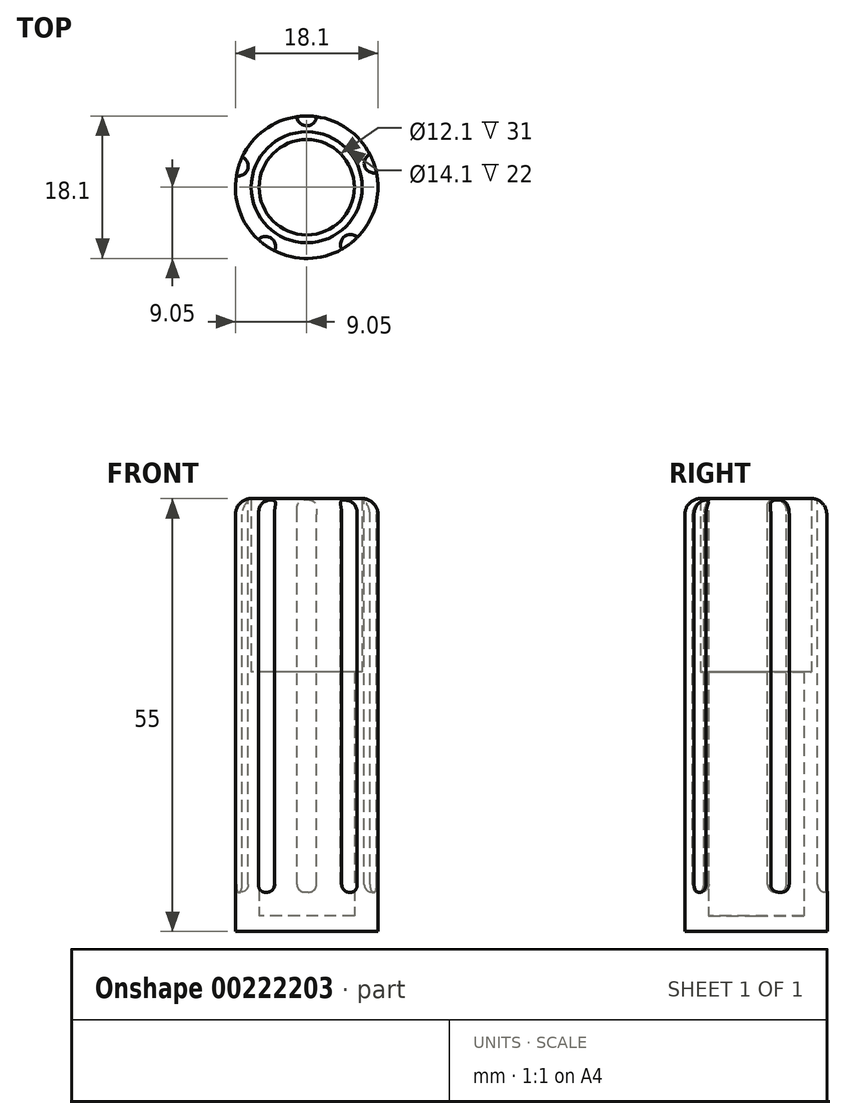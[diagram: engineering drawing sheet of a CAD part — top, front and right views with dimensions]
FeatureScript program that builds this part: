
annotation { "Feature Type Name" : "Feature", "Feature Type Description" : "" }
export const myFeature = defineFeature(function(context is Context, id is Id, definition is map)
    precondition{}
    {
        {
            var Q0;
            Q0=qCreatedBy(makeId("Top.planeOp"),FACE);
            var sketch = newSketch(context, id + "F0", { "sketchPlane" : qUnion([Q0])});
            skCircle(sketch, "E0", {"center": v(0, 0) * mm, "radius": 6.05 * mm});
            skCircle(sketch, "E1", {"center": v(0, 0) * mm, "radius": 7.05 * mm});
            skCircle(sketch, "E2", {"center": v(0, 0) * mm, "radius": 9.05 * mm});
            skCircle(sketch, "E3", {"center": v(0, 9.05) * mm, "radius": 1.25 * mm});
            skCircle(sketch, "E4.1.0", {"center": v(-8.68, 2.69) * mm, "radius": 1.25 * mm});
            skCircle(sketch, "E4.2.0", {"center": v(-5.22, -7.5) * mm, "radius": 1.25 * mm});
            skCircle(sketch, "E4.3.0", {"center": v(5.54, -7.27) * mm, "radius": 1.25 * mm});
            skCircle(sketch, "E4.4.0", {"center": v(8.55, 3.06) * mm, "radius": 1.25 * mm});
            skPoint(sketch, "E4.center", {"position": v(0, -0.05) * mm});
            skLineSegment(sketch, "E4.anchor1", {"start": v(0, -0.05) * mm, "end": v(0, 9.05) * mm, "construction": true});
            skLineSegment(sketch, "E4.anchor2", {"start": v(0, -0.05) * mm, "end": v(8.55, 3.06) * mm, "construction": true});
            skSolve(sketch);
        }
        {
            var Q0;
            Q0=makeQuery(id+"F0.imprint","IMPRINT",FACE,{"disambiguationData":[TD([[makeQuery(id+"F0.imprint","IMPRINT",EDGE,{"derivedFrom":sQuery(id+"F0.wireOp",EDGE,"E0")}),1.0]])]});
            var Q1;
            Q1=makeQuery(id+"F0.imprint","IMPRINT",FACE,{"disambiguationData":[TD([[makeQuery(id+"F0.imprint","IMPRINT",EDGE,{"derivedFrom":sQuery(id+"F0.wireOp",EDGE,"E0")}),-1.0]])]});
            var Q2;
            Q2=makeQuery(id+"F0.imprint","IMPRINT",FACE,{"disambiguationData":[TD([[makeQuery(id+"F0.imprint","IMPRINT",EDGE,{"derivedFrom":sQuery(id+"F0.wireOp",EDGE,"E1")}),-1.0]])]});
            extrude(context, id + "F1", {"entities" : qUnion([Q0, Q1, Q2]), "oppositeDirection" : true, "depth" : 2 * mm});
        }
        {
            var Q0;
            Q0=makeQuery(id+"F0.imprint","IMPRINT",FACE,{"disambiguationData":[TD([[makeQuery(id+"F0.imprint","IMPRINT",EDGE,{"derivedFrom":sQuery(id+"F0.wireOp",EDGE,"E0")}),-1.0]])]});
            extrude(context, id + "F2", {"entities" : qUnion([Q0]), "operationType" : NewBodyOperationType.ADD, "depth" : 31 * mm});
        }
        {
            var Q0;
            Q0=makeQuery(id+"F0.imprint","IMPRINT",FACE,{"disambiguationData":[TD([[makeQuery(id+"F0.imprint","IMPRINT",EDGE,{"derivedFrom":sQuery(id+"F0.wireOp",EDGE,"E1")}),-1.0]])]});
            extrude(context, id + "F3", {"entities" : qUnion([Q0]), "operationType" : NewBodyOperationType.ADD, "depth" : 53 * mm});
        }
        {
            var Q0;
            {var subQ0=sQuery(id+"F0.wireOp",EDGE,"E2");Q0=makeQuery(id+"F3.opExtrude","CAP_EDGE",EDGE,{"disambiguationData":[OSD([subQ0]),TDD([makeQuery(id+"F0.imprint","IMPRINT",EDGE,{"disambiguationData":[TD([[makeQuery(id+"F0.imprint","INTERSECT",VERTEX,{"disambiguationData":[OD(1.0)],"derivedFrom":[subQ0,sQuery(id+"F0.wireOp",EDGE,"E4.1.0")]}),-1.0]])],"derivedFrom":subQ0})])],"isStart":false});}
            var Q1;
            {var subQ0=sQuery(id+"F0.wireOp",EDGE,"E2");Q1=makeQuery(id+"F3.opExtrude","CAP_EDGE",EDGE,{"disambiguationData":[OSD([subQ0]),TDD([makeQuery(id+"F0.imprint","IMPRINT",EDGE,{"disambiguationData":[TD([[makeQuery(id+"F0.imprint","INTERSECT",VERTEX,{"disambiguationData":[OD(1.0)],"derivedFrom":[subQ0,sQuery(id+"F0.wireOp",EDGE,"E4.2.0")]}),-1.0]])],"derivedFrom":subQ0})])],"isStart":false});}
            var Q2;
            {var subQ0=sQuery(id+"F0.wireOp",EDGE,"E2");Q2=makeQuery(id+"F3.opExtrude","CAP_EDGE",EDGE,{"disambiguationData":[OSD([subQ0]),TDD([makeQuery(id+"F0.imprint","IMPRINT",EDGE,{"disambiguationData":[TD([[makeQuery(id+"F0.imprint","INTERSECT",VERTEX,{"disambiguationData":[OD(1.0)],"derivedFrom":[subQ0,sQuery(id+"F0.wireOp",EDGE,"E3")]}),-1.0]])],"derivedFrom":subQ0})])],"isStart":false});}
            var Q3;
            {var subQ0=sQuery(id+"F0.wireOp",EDGE,"E2");Q3=makeQuery(id+"F3.opExtrude","CAP_EDGE",EDGE,{"disambiguationData":[OSD([subQ0]),TDD([makeQuery(id+"F0.imprint","IMPRINT",EDGE,{"disambiguationData":[TD([[makeQuery(id+"F0.imprint","INTERSECT",VERTEX,{"disambiguationData":[OD(0.0)],"derivedFrom":[subQ0,sQuery(id+"F0.wireOp",EDGE,"E4.4.0")]}),-1.0]])],"derivedFrom":subQ0})])],"isStart":false});}
            var Q4;
            {var subQ0=sQuery(id+"F0.wireOp",EDGE,"E2");Q4=makeQuery(id+"F3.opExtrude","CAP_EDGE",EDGE,{"disambiguationData":[OSD([subQ0]),TDD([makeQuery(id+"F0.imprint","IMPRINT",EDGE,{"disambiguationData":[TD([[makeQuery(id+"F0.imprint","INTERSECT",VERTEX,{"disambiguationData":[OD(1.0)],"derivedFrom":[subQ0,sQuery(id+"F0.wireOp",EDGE,"E4.4.0")]}),1.0]])],"derivedFrom":subQ0})])],"isStart":false});}
            fillet(context, id + "F4", {"entities" : qUnion([Q0, Q1, Q2, Q3, Q4]), "radius" : 2 * mm, "tangentPropagation" : true, "allowEdgeOverflow" : false});
        }
        {
            var Q0;
            {var subQ0=sQuery(id+"F0.wireOp",EDGE,"E4.4.0");var subQ1=sQuery(id+"F0.wireOp",EDGE,"E2");var subQ2=makeQuery(id+"F0.imprint","INTERSECT",VERTEX,{"disambiguationData":[OD(0.0)],"derivedFrom":[subQ1,subQ0]});Q0=makeQuery(id+"F0.imprint","IMPRINT",FACE,{"disambiguationData":[TD([[makeQuery(id+"F0.imprint","IMPRINT",EDGE,{"disambiguationData":[TD([[subQ2,1.0]])],"derivedFrom":subQ1}),1.0]])]});}
            var Q1;
            {var subQ0=sQuery(id+"F0.wireOp",EDGE,"E4.3.0");var subQ1=sQuery(id+"F0.wireOp",EDGE,"E2");var subQ2=makeQuery(id+"F0.imprint","INTERSECT",VERTEX,{"disambiguationData":[OD(0.0)],"derivedFrom":[subQ1,subQ0]});Q1=makeQuery(id+"F0.imprint","IMPRINT",FACE,{"disambiguationData":[TD([[makeQuery(id+"F0.imprint","IMPRINT",EDGE,{"disambiguationData":[TD([[subQ2,-1.0]])],"derivedFrom":subQ1}),1.0]])]});}
            var Q2;
            {var subQ0=sQuery(id+"F0.wireOp",EDGE,"E4.2.0");var subQ1=sQuery(id+"F0.wireOp",EDGE,"E2");var subQ2=makeQuery(id+"F0.imprint","INTERSECT",VERTEX,{"disambiguationData":[OD(0.0)],"derivedFrom":[subQ1,subQ0]});Q2=makeQuery(id+"F0.imprint","IMPRINT",FACE,{"disambiguationData":[TD([[makeQuery(id+"F0.imprint","IMPRINT",EDGE,{"disambiguationData":[TD([[subQ2,-1.0]])],"derivedFrom":subQ1}),1.0]])]});}
            var Q3;
            {var subQ0=sQuery(id+"F0.wireOp",EDGE,"E4.1.0");var subQ1=sQuery(id+"F0.wireOp",EDGE,"E2");var subQ2=makeQuery(id+"F0.imprint","INTERSECT",VERTEX,{"disambiguationData":[OD(0.0)],"derivedFrom":[subQ1,subQ0]});Q3=makeQuery(id+"F0.imprint","IMPRINT",FACE,{"disambiguationData":[TD([[makeQuery(id+"F0.imprint","IMPRINT",EDGE,{"disambiguationData":[TD([[subQ2,-1.0]])],"derivedFrom":subQ1}),1.0]])]});}
            var Q4;
            {var subQ0=sQuery(id+"F0.wireOp",EDGE,"E3");var subQ1=sQuery(id+"F0.wireOp",EDGE,"E2");var subQ2=makeQuery(id+"F0.imprint","INTERSECT",VERTEX,{"disambiguationData":[OD(0.0)],"derivedFrom":[subQ1,subQ0]});Q4=makeQuery(id+"F0.imprint","IMPRINT",FACE,{"disambiguationData":[TD([[makeQuery(id+"F0.imprint","IMPRINT",EDGE,{"disambiguationData":[TD([[subQ2,-1.0]])],"derivedFrom":subQ1}),1.0]])]});}
            extrude(context, id + "F5", {"entities" : qUnion([Q0, Q1, Q2, Q3, Q4]), "operationType" : NewBodyOperationType.ADD, "depth" : 3 * mm});
        }
        {
            var Q0;
            Q0=makeQuery(id+"F5.opExtrude","CAP_EDGE",EDGE,{"disambiguationData":[OSD([sQuery(id+"F0.wireOp",EDGE,"E4.2.0")])],"isStart":false});
            var Q1;
            Q1=makeQuery(id+"F5.opExtrude","CAP_EDGE",EDGE,{"disambiguationData":[OSD([sQuery(id+"F0.wireOp",EDGE,"E4.1.0")])],"isStart":false});
            var Q2;
            Q2=makeQuery(id+"F5.opExtrude","CAP_EDGE",EDGE,{"disambiguationData":[OSD([sQuery(id+"F0.wireOp",EDGE,"E4.3.0")])],"isStart":false});
            var Q3;
            Q3=makeQuery(id+"F5.opExtrude","CAP_EDGE",EDGE,{"disambiguationData":[OSD([sQuery(id+"F0.wireOp",EDGE,"E4.4.0")])],"isStart":false});
            var Q4;
            Q4=makeQuery(id+"F5.opExtrude","CAP_EDGE",EDGE,{"disambiguationData":[OSD([sQuery(id+"F0.wireOp",EDGE,"E3")])],"isStart":false});
            fillet(context, id + "F6", {"entities" : qUnion([Q0, Q1, Q2, Q3, Q4]), "radius" : 1 * mm, "tangentPropagation" : true, "allowEdgeOverflow" : false});
        }
        {
            var Q0;
            {var subQ0=sQuery(id+"F0.wireOp",EDGE,"E4.2.0");var subQ1=sQuery(id+"F0.wireOp",EDGE,"E2");var subQ2=makeQuery(id+"F0.imprint","INTERSECT",VERTEX,{"disambiguationData":[OD(0.0)],"derivedFrom":[subQ1,subQ0]});Q0=makeQuery(id+"F0.imprint","IMPRINT",FACE,{"disambiguationData":[TD([[makeQuery(id+"F0.imprint","IMPRINT",EDGE,{"disambiguationData":[TD([[subQ2,-1.0]])],"derivedFrom":subQ1}),1.0]])]});}
            var Q1;
            {var subQ0=sQuery(id+"F0.wireOp",EDGE,"E4.3.0");var subQ1=sQuery(id+"F0.wireOp",EDGE,"E2");var subQ2=makeQuery(id+"F0.imprint","INTERSECT",VERTEX,{"disambiguationData":[OD(0.0)],"derivedFrom":[subQ1,subQ0]});Q1=makeQuery(id+"F0.imprint","IMPRINT",FACE,{"disambiguationData":[TD([[makeQuery(id+"F0.imprint","IMPRINT",EDGE,{"disambiguationData":[TD([[subQ2,-1.0]])],"derivedFrom":subQ1}),1.0]])]});}
            var Q2;
            {var subQ0=sQuery(id+"F0.wireOp",EDGE,"E4.4.0");var subQ1=sQuery(id+"F0.wireOp",EDGE,"E2");var subQ2=makeQuery(id+"F0.imprint","INTERSECT",VERTEX,{"disambiguationData":[OD(0.0)],"derivedFrom":[subQ1,subQ0]});Q2=makeQuery(id+"F0.imprint","IMPRINT",FACE,{"disambiguationData":[TD([[makeQuery(id+"F0.imprint","IMPRINT",EDGE,{"disambiguationData":[TD([[subQ2,1.0]])],"derivedFrom":subQ1}),1.0]])]});}
            var Q3;
            {var subQ0=sQuery(id+"F0.wireOp",EDGE,"E3");var subQ1=sQuery(id+"F0.wireOp",EDGE,"E2");var subQ2=makeQuery(id+"F0.imprint","INTERSECT",VERTEX,{"disambiguationData":[OD(0.0)],"derivedFrom":[subQ1,subQ0]});Q3=makeQuery(id+"F0.imprint","IMPRINT",FACE,{"disambiguationData":[TD([[makeQuery(id+"F0.imprint","IMPRINT",EDGE,{"disambiguationData":[TD([[subQ2,-1.0]])],"derivedFrom":subQ1}),1.0]])]});}
            var Q4;
            {var subQ0=sQuery(id+"F0.wireOp",EDGE,"E4.1.0");var subQ1=sQuery(id+"F0.wireOp",EDGE,"E2");var subQ2=makeQuery(id+"F0.imprint","INTERSECT",VERTEX,{"disambiguationData":[OD(0.0)],"derivedFrom":[subQ1,subQ0]});Q4=makeQuery(id+"F0.imprint","IMPRINT",FACE,{"disambiguationData":[TD([[makeQuery(id+"F0.imprint","IMPRINT",EDGE,{"disambiguationData":[TD([[subQ2,-1.0]])],"derivedFrom":subQ1}),1.0]])]});}
            extrude(context, id + "F7", {"entities" : qUnion([Q0, Q1, Q2, Q3, Q4]), "operationType" : NewBodyOperationType.ADD, "oppositeDirection" : true, "depth" : 2 * mm});
        }
    });
